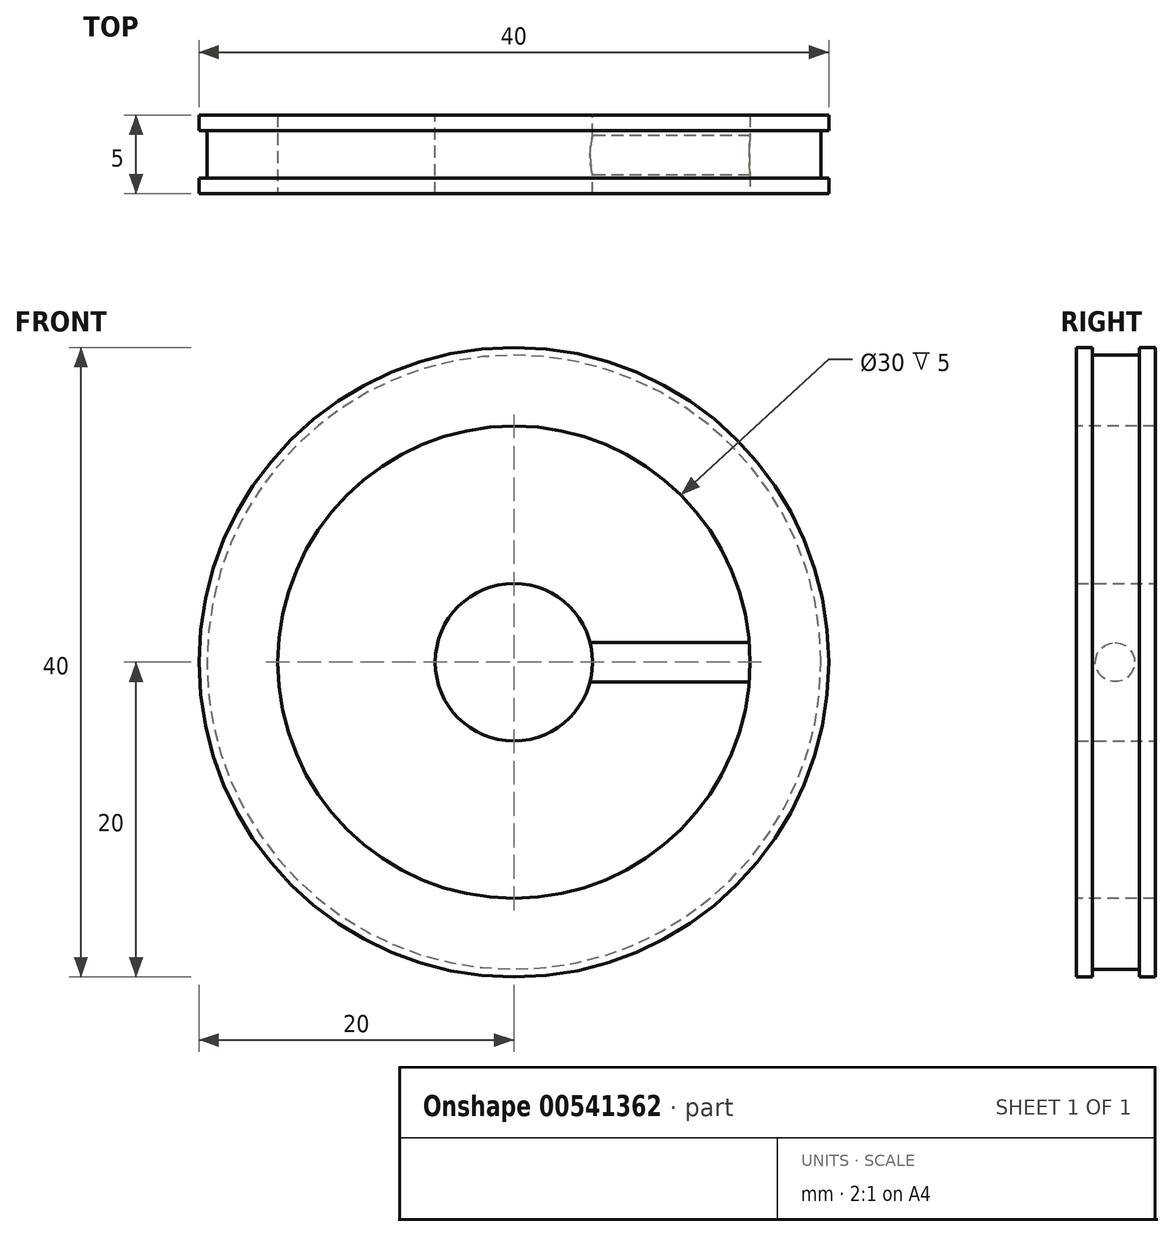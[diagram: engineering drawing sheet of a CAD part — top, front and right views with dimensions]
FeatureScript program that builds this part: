
annotation { "Feature Type Name" : "Feature", "Feature Type Description" : "" }
export const myFeature = defineFeature(function(context is Context, id is Id, definition is map)
    precondition{}
    {
        {
            var Q0;
            Q0=qCreatedBy(makeId("Front.planeOp"),FACE);
            var sketch = newSketch(context, id + "F0", { "sketchPlane" : qUnion([Q0])});
            skCircle(sketch, "E0", {"center": v(0, 0) * mm, "radius": 20 * mm});
            skSolve(sketch);
        }
        {
            var Q0;
            Q0=qSketchRegion(id+"F0",true);
            extrude(context, id + "F1", {"entities" : qUnion([Q0]), "depth" : 5 * mm, "offsetDistance" : 25 * mm});
        }
        {
            var Q0;
            Q0=makeQuery(id+"F1.opExtrude","CAP_FACE",FACE,{"disambiguationData":[OSD([sQuery(id+"F0.wireOp",EDGE,"E0")])],"isStart":false});
            var sketch = newSketch(context, id + "F2", { "sketchPlane" : qUnion([Q0])});
            skCircle(sketch, "E1", {"center": v(0, 0) * mm, "radius": 15 * mm});
            skSolve(sketch);
        }
        {
            var Q0;
            Q0=qSketchRegion(id+"F2",true);
            extrude(context, id + "F3", {"entities" : qUnion([Q0]), "operationType" : NewBodyOperationType.REMOVE, "oppositeDirection" : true, "depth" : 5 * mm, "offsetDistance" : 25 * mm});
        }
        {
            var Q0;
            Q0=qCreatedBy(makeId("Front.planeOp"),FACE);
            var sketch = newSketch(context, id + "F4", { "sketchPlane" : qUnion([Q0])});
            skCircle(sketch, "E2", {"center": v(0, 0) * mm, "radius": 5 * mm});
            skSolve(sketch);
        }
        {
            var Q0;
            Q0=qSketchRegion(id+"F4",true);
            extrude(context, id + "F5", {"entities" : qUnion([Q0]), "depth" : 5 * mm, "offsetDistance" : 25 * mm});
        }
        {
            var Q0;
            Q0=qCreatedBy(makeId("Right.planeOp"),FACE);
            var sketch = newSketch(context, id + "F6", { "sketchPlane" : qUnion([Q0])});
            skCircle(sketch, "E3", {"center": v(-2.55, 0) * mm, "radius": 1.25 * mm});
            skSolve(sketch);
        }
        {
            var Q0;
            Q0=qSketchRegion(id+"F6",true);
            var Q1;
            Q1=sQuery(id+"F6.wireOp",EDGE,"E3");
            extrude(context, id + "F7", {"entities" : qUnion([Q0]), "operationType" : NewBodyOperationType.ADD, "surfaceEntities" : qUnion([Q1]), "depth" : 19 * mm, "offsetDistance" : 25 * mm});
        }
        {
            var Q0;
            Q0=qCreatedBy(makeId("Right.planeOp"),FACE);
            var sketch = newSketch(context, id + "F8", { "sketchPlane" : qUnion([Q0])});
            skLineSegment(sketch, "E4.0", {"start": v(-5, -20) * mm, "end": v(-5, 20) * mm});
            skLineSegment(sketch, "E5.top", {"start": v(-4, 19.5) * mm, "end": v(-1, 19.5) * mm});
            skLineSegment(sketch, "E5.left", {"start": v(-4, 20) * mm, "end": v(-4, 19.5) * mm});
            skLineSegment(sketch, "E5.right", {"start": v(-1, 20) * mm, "end": v(-1, 19.5) * mm});
            skLineSegment(sketch, "E6", {"start": v(-5, 20) * mm, "end": v(-4, 20) * mm, "construction": true});
            skLineSegment(sketch, "E7", {"start": v(-1, 20) * mm, "end": v(0, 20) * mm, "construction": true});
            skLineSegment(sketch, "E8", {"start": v(-4, 20) * mm, "end": v(-1, 20) * mm});
            skSolve(sketch);
        }
        {
            var Q0;
            Q0=qSketchRegion(id+"F8",true);
            var Q1;
            Q1=makeQuery(id+"F1.opExtrude","SWEPT_FACE",FACE,{"disambiguationData":[OSD([sQuery(id+"F0.wireOp",EDGE,"E0")])]});
            revolve(context, id + "F9", {"operationType" : NewBodyOperationType.REMOVE, "entities" : qUnion([Q0]), "axis" : qUnion([Q1]), "revolveType" : RevolveType.FULL, "oppositeDirection" : true});
        }
    });
